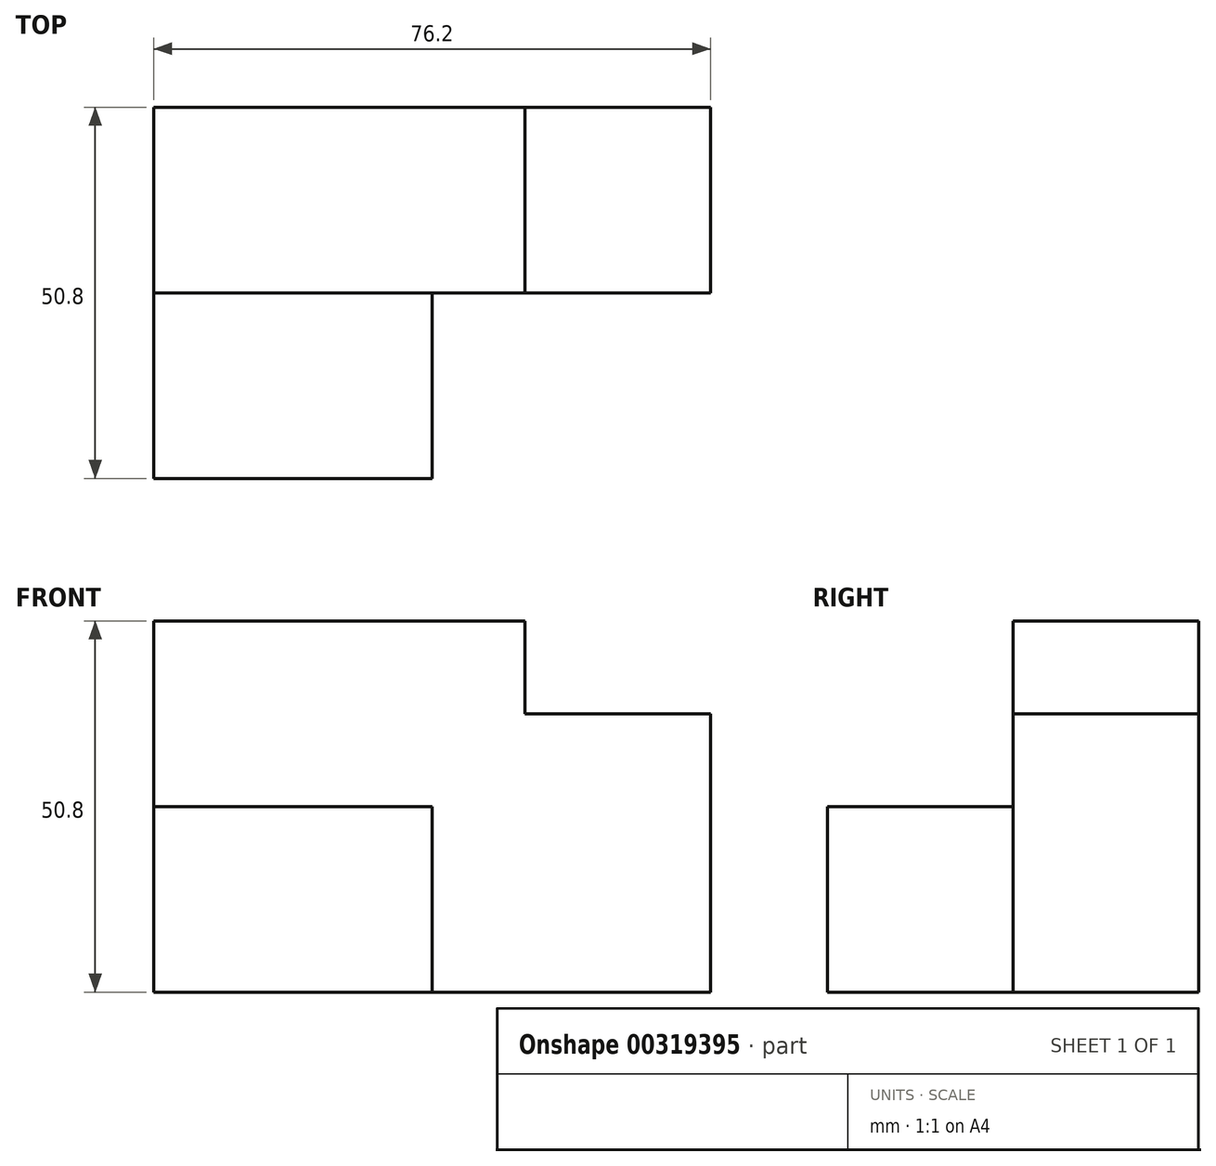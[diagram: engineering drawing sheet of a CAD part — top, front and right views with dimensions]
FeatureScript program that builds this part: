
annotation { "Feature Type Name" : "Feature", "Feature Type Description" : "" }
export const myFeature = defineFeature(function(context is Context, id is Id, definition is map)
    precondition{}
    {
        {
            var Q0;
            Q0=qCreatedBy(makeId("Right.planeOp"),FACE);
            var sketch = newSketch(context, id + "F0", { "sketchPlane" : qUnion([Q0])});
            skLineSegment(sketch, "E0", {"start": v(43.14, -43.5) * mm, "end": v(-7.66, -43.5) * mm});
            skLineSegment(sketch, "E1", {"start": v(-7.66, -43.5) * mm, "end": v(-7.66, -18.1) * mm});
            skLineSegment(sketch, "E2", {"start": v(-7.66, -18.1) * mm, "end": v(17.74, -18.1) * mm});
            skLineSegment(sketch, "E3", {"start": v(17.74, -18.1) * mm, "end": v(17.74, 7.3) * mm});
            skLineSegment(sketch, "E4", {"start": v(17.74, 7.3) * mm, "end": v(43.14, 7.3) * mm});
            skLineSegment(sketch, "E5", {"start": v(43.14, 7.3) * mm, "end": v(43.14, -43.5) * mm});
            skSolve(sketch);
        }
        {
            var Q0;
            Q0=makeQuery(id+"F0.imprint","IMPRINT",FACE,{"disambiguationData":[TD([[makeQuery(id+"F0.imprint","IMPRINT",EDGE,{"derivedFrom":sQuery(id+"F0.wireOp",EDGE,"E0")}),-1.0]])]});
            extrude(context, id + "F1", {"entities" : qUnion([Q0]), "depth" : 76.2 * mm});
        }
        {
            var Q0;
            Q0=makeQuery(id+"F1.opExtrude","SWEPT_FACE",FACE,{"disambiguationData":[OSD([sQuery(id+"F0.wireOp",EDGE,"E1")])]});
            var sketch = newSketch(context, id + "F2", { "sketchPlane" : qUnion([Q0])});
            skLineSegment(sketch, "E6", {"start": v(38.1, -18.1) * mm, "end": v(38.1, -43.5) * mm});
            skSolve(sketch);
        }
        {
            var Q0;
            {var subQ0=sQuery(id+"F2.wireOp",EDGE,"E6");Q0=makeQuery(id+"F2.imprint","IMPRINT",FACE,{"disambiguationData":[TD([[makeQuery(id+"F2.imprint","IMPRINT",EDGE,{"derivedFrom":subQ0}),1.0]])]});}
            extrude(context, id + "F3", {"entities" : qUnion([Q0]), "operationType" : NewBodyOperationType.REMOVE, "oppositeDirection" : true, "depth" : 25.4 * mm});
        }
        {
            var Q0;
            Q0=makeQuery(id+"F3.boolean.opBoolean","MERGE",FACE,{"derivedFrom":[makeQuery(id+"F1.opExtrude","SWEPT_FACE",FACE,{"disambiguationData":[OSD([sQuery(id+"F0.wireOp",EDGE,"E3")])]}),makeQuery(id+"F3.opExtrude","CAP_FACE",FACE,{"disambiguationData":[OSD([sQuery(id+"F0.wireOp",EDGE,"E0"),sQuery(id+"F0.wireOp",EDGE,"E1"),sQuery(id+"F0.wireOp",EDGE,"E2"),sQuery(id+"F2.wireOp",EDGE,"E6")])],"isStart":false})]});
            var sketch = newSketch(context, id + "F4", { "sketchPlane" : qUnion([Q0])});
            skLineSegment(sketch, "E7", {"start": v(50.8, 7.3) * mm, "end": v(50.8, -5.4) * mm});
            skLineSegment(sketch, "E8", {"start": v(50.8, -5.4) * mm, "end": v(76.2, -5.4) * mm});
            skSolve(sketch);
        }
        {
            var Q0;
            {var subQ0=sQuery(id+"F4.wireOp",EDGE,"E7");Q0=makeQuery(id+"F4.imprint","IMPRINT",FACE,{"disambiguationData":[TD([[makeQuery(id+"F4.imprint","IMPRINT",EDGE,{"derivedFrom":subQ0}),1.0]])]});}
            extrude(context, id + "F5", {"entities" : qUnion([Q0]), "operationType" : NewBodyOperationType.REMOVE, "endBound" : BoundingType.THROUGH_ALL, "oppositeDirection" : true, "depth" : 25.4 * mm});
        }
    });
